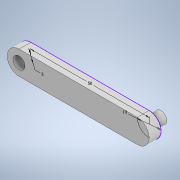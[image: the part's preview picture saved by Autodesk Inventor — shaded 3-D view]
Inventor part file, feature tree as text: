
AUTODESK INVENTOR PART (.ipt)
format: ipt  version: 2022 (Build 260153000, 153)  size: 107,520 bytes
history: native  units: mm
features: extrude x2, sketch x1
ambient origin geometry x8: Origin, YZ Plane, XZ Plane, XY Plane, X Axis, Y Axis, Z Axis, Center Point
bodies: Solid1 (feature_tree)
feature tree (3):
  sketch  "Sketch1"  dims[d0=50.0mm d1=10.0mm d2=5.0mm d3=5.0mm d4=0.0mm d5=5.0mm d6=0.0mm]
  extrude  "Extrusion1"  Depth=10.0mm
  extrude  "Extrusion2"  Depth=5.0mm
